# Revit family: ASL_Door Suite_Stile_125mm
name_source: partatom
category: Detail Items
revit_build: Autodesk Revit 2018 (Build: 20170223_1515(x64)
units: mm (PartAtom-declared; Revit-internal decimal feet)

## family parameters
Rotate with component = No
Section Shape = Not Defined
Shared = Yes

## types (4) — shared parameters
Manufacturer = Aluminate Solutions Limited
Technical Info = www.aluminate.nz

## per-type parameters (varying)
| type | ASL_Woolpile_1 | ASL_Woolpile_2 | Infill for Closing Stile | Type Comments |
| Lockset Stile Hinge Door 125mm | Yes | No | No | ASL Door Suite 125mm Lockset Stile Hinge Door |
| Hinge Stile Hinge Door 125mm | No | No | Yes | ASL Door Suite 125mm Hinge Stile Hinge Door |
| Lockset Stile Double Action Hinge, Pviot and Sliding Door 125mm | Yes | Yes | No | ASL Door Suite 125mm Lockset Stile Double Action Hinge, Pviot and Sliding Door |
| Closing Stile Pivot and Sliding Door 125mm | Yes | Yes | Yes | ASL Door Suite 125mm Closing Stile Pivot and Sliding Door |

## geometry (parser evidence)
native form markers: Sweep x4
no freeform markers — native parametric forms only
